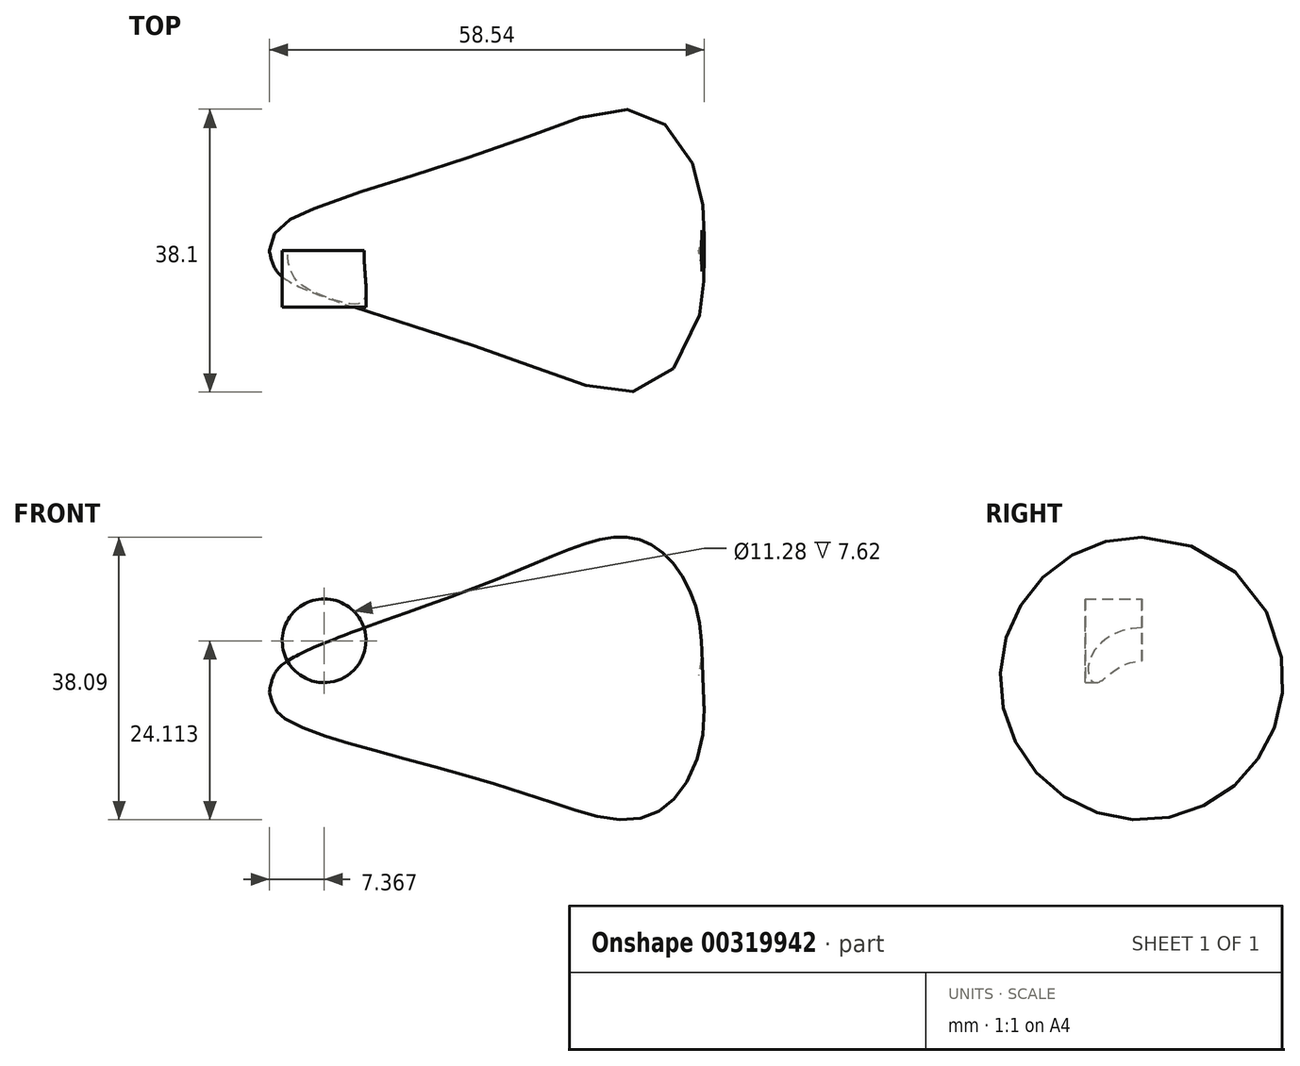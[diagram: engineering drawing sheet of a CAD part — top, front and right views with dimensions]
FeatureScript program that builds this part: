
annotation { "Feature Type Name" : "Feature", "Feature Type Description" : "" }
export const myFeature = defineFeature(function(context is Context, id is Id, definition is map)
    precondition{}
    {
        {
            var Q0;
            Q0=qCreatedBy(makeId("Front.planeOp"),FACE);
            var sketch = newSketch(context, id + "F0", { "sketchPlane" : qUnion([Q0])});
            skFitSpline(sketch, "E0", {"points": [v(-58.16, 15.32) * mm, v(-55.4, 19.73) * mm, v(-26.3, 31.02) * mm, v(-7.72, 35.64) * mm, v(0, 20.49) * mm, v(-15.18, 0) * mm, v(-43.8, 1.46) * mm, v(-56.63, 2.46) * mm, v(-58.16, 15.32) * mm]});
            skLineSegment(sketch, "E1", {"start": v(-58.16, 15.32) * mm, "end": v(-0.38, 17.56) * mm});
            skSolve(sketch);
        }
        {
            var Q0;
            {var subQ0=sQuery(id+"F0.wireOp",EDGE,"E1");Q0=makeQuery(id+"F0.imprint","IMPRINT",FACE,{"disambiguationData":[TD([[makeQuery(id+"F0.imprint","IMPRINT",EDGE,{"derivedFrom":subQ0}),1.0]])]});}
            var Q1;
            Q1=sQuery(id+"F0.wireOp",EDGE,"E1");
            revolve(context, id + "F1", {"entities" : qUnion([Q0]), "axis" : qUnion([Q1]), "revolveType" : RevolveType.FULL});
        }
        {
            var Q0;
            Q0=qCreatedBy(makeId("Front.planeOp"),FACE);
            var sketch = newSketch(context, id + "F2", { "sketchPlane" : qUnion([Q0])});
            skCircle(sketch, "E2", {"center": v(-50.8, 22.23) * mm, "radius": 5.64 * mm});
            skLineSegment(sketch, "E3", {"start": v(-58.54, 15.47) * mm, "end": v(0, 15.47) * mm});
            skCircle(sketch, "E4.MirrorC", {"center": v(-50.8, 8.7) * mm, "radius": 5.64 * mm});
            skSolve(sketch);
        }
        {
            var Q0;
            Q0=makeQuery(id+"F2.imprint","IMPRINT",FACE,{"disambiguationData":[TD([[makeQuery(id+"F2.imprint","IMPRINT",EDGE,{"derivedFrom":sQuery(id+"F2.wireOp",EDGE,"E2")}),1.0]])]});
            var Q1;
            Q1=makeQuery(id+"F2.imprint","IMPRINT",FACE,{"disambiguationData":[TD([[makeQuery(id+"F2.imprint","IMPRINT",EDGE,{"derivedFrom":sQuery(id+"F2.wireOp",EDGE,"E4.MirrorC")}),-1.0]])]});
            extrude(context, id + "F3", {"entities" : qUnion([Q0, Q1]), "operationType" : NewBodyOperationType.ADD, "depth" : 7.62 * mm});
        }
    });
